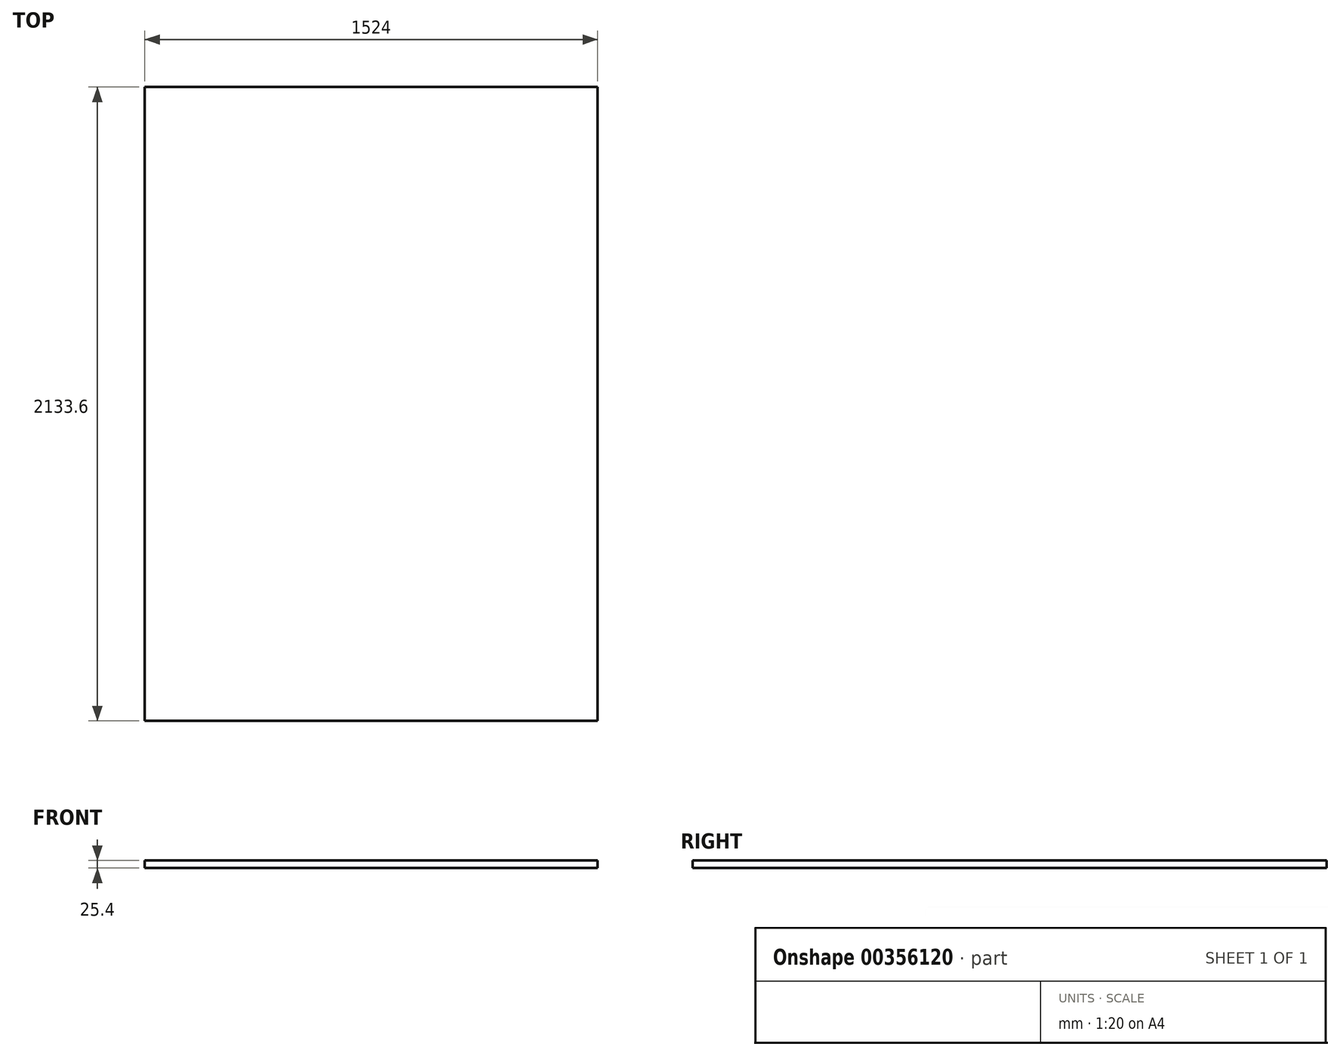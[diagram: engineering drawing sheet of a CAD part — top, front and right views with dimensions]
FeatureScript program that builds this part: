
annotation { "Feature Type Name" : "Feature", "Feature Type Description" : "" }
export const myFeature = defineFeature(function(context is Context, id is Id, definition is map)
    precondition{}
    {
        {
            var Q0;
            Q0=qCreatedBy(makeId("Top.planeOp"),FACE);
            var sketch = newSketch(context, id + "F0", { "sketchPlane" : qUnion([Q0])});
            skLineSegment(sketch, "E0.bottom", {"start": v(-762, 1066.8) * mm, "end": v(762, 1066.8) * mm});
            skLineSegment(sketch, "E0.top", {"start": v(-762, -1066.8) * mm, "end": v(762, -1066.8) * mm});
            skLineSegment(sketch, "E0.left", {"start": v(-762, 1066.8) * mm, "end": v(-762, -1066.8) * mm});
            skLineSegment(sketch, "E0.right", {"start": v(762, 1066.8) * mm, "end": v(762, -1066.8) * mm});
            skPoint(sketch, "E0.middle", {"position": v(0, 0) * mm});
            skSolve(sketch);
        }
        {
            var Q0;
            Q0=makeQuery(id+"F0.imprint","IMPRINT",FACE,{"disambiguationData":[TD([[makeQuery(id+"F0.imprint","IMPRINT",EDGE,{"derivedFrom":sQuery(id+"F0.wireOp",EDGE,"E0.bottom")}),-1.0]])]});
            extrude(context, id + "F1", {"entities" : qUnion([Q0]), "depth" : 25.4 * mm});
        }
    });
